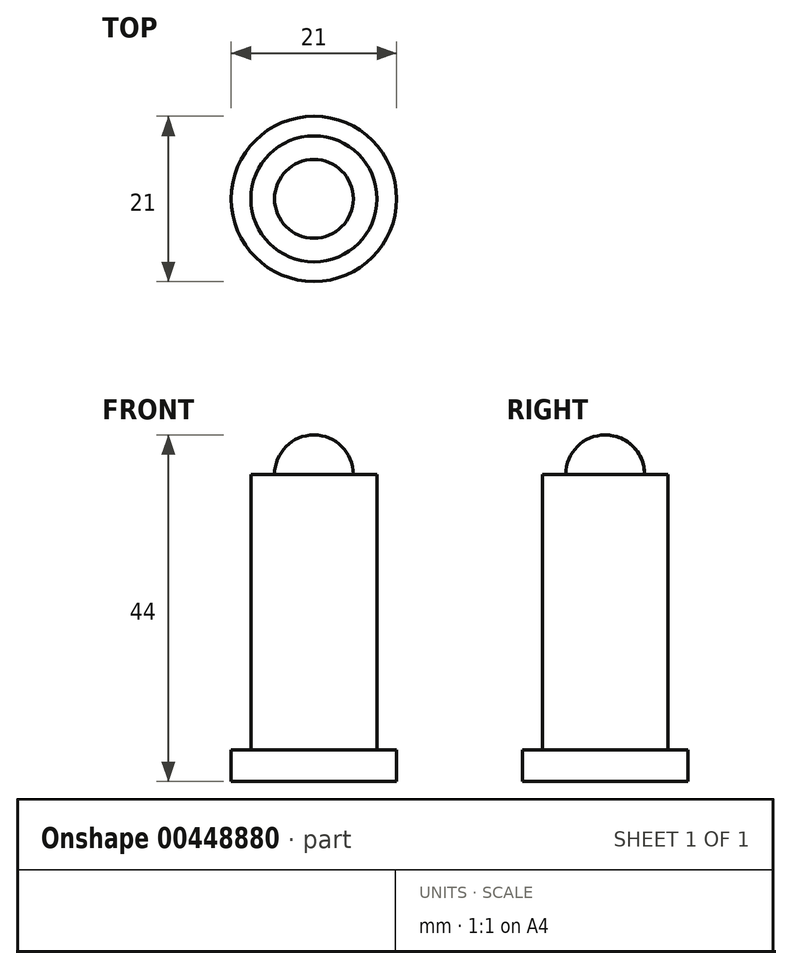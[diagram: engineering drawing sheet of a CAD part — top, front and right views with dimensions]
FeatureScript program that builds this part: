
annotation { "Feature Type Name" : "Feature", "Feature Type Description" : "" }
export const myFeature = defineFeature(function(context is Context, id is Id, definition is map)
    precondition{}
    {
        {
            var Q0;
            Q0=qCreatedBy(makeId("Top.planeOp"),FACE);
            var sketch = newSketch(context, id + "F0", { "sketchPlane" : qUnion([Q0])});
            skCircle(sketch, "E0", {"center": v(0, 0) * mm, "radius": 10.5 * mm});
            skSolve(sketch);
        }
        {
            var Q0;
            Q0=qSketchRegion(id+"F0",true);
            extrude(context, id + "F1", {"entities" : qUnion([Q0]), "depth" : 4 * mm});
        }
        {
            var Q0;
            Q0=qCreatedBy(makeId("Top.planeOp"),FACE);
            var sketch = newSketch(context, id + "F2", { "sketchPlane" : qUnion([Q0])});
            skCircle(sketch, "E1", {"center": v(0, 0) * mm, "radius": 8 * mm});
            skSolve(sketch);
        }
        {
            var Q0;
            Q0=qSketchRegion(id+"F2",true);
            extrude(context, id + "F3", {"entities" : qUnion([Q0]), "operationType" : NewBodyOperationType.ADD, "depth" : 39 * mm});
        }
        {
            var Q0;
            Q0=qCreatedBy(makeId("Right.planeOp"),FACE);
            var sketch = newSketch(context, id + "F4", { "sketchPlane" : qUnion([Q0])});
            skLineSegment(sketch, "E2", {"start": v(0, 44) * mm, "end": v(0, 39) * mm});
            skLineSegment(sketch, "E3", {"start": v(0, 39) * mm, "end": v(5, 39) * mm});
            skArc(sketch, "E4", {"start": v(5, 39) * mm, "mid": v(3.54, 42.54) * mm, "end": v(0, 44) * mm});
            skSolve(sketch);
        }
        {
            var Q0;
            Q0=makeQuery(id+"F4.imprint","IMPRINT",FACE,{"disambiguationData":[TD([[makeQuery(id+"F4.imprint","IMPRINT",EDGE,{"derivedFrom":sQuery(id+"F4.wireOp",EDGE,"E2")}),1.0]])]});
            var Q1;
            {var subQ4=sQuery(id+"F4.wireOp",EDGE,"bCaXd63Z-sSvQ-xuQP-ZVX1-OTuKCmXqE8nU");Q1=makeQuery(id+"F4.imprint","IMPRINT",FACE,{"disambiguationData":[TD([[makeQuery(id+"F4.imprint","IMPRINT",EDGE,{"derivedFrom":subQ4}),1.0]])]});}
            var Q2;
            {var subQ3=sQuery(id+"F4.wireOp",EDGE,"1d30ehnV-xLIY-fLZD-29Qb-ZKUb7VrrrgXH");Q2=makeQuery(id+"F4.imprint","IMPRINT",FACE,{"disambiguationData":[TD([[makeQuery(id+"F4.imprint","IMPRINT",EDGE,{"derivedFrom":subQ3}),1.0]])]});}
            var Q3;
            Q3=sQuery(id+"F4.wireOp",EDGE,"E2");
            revolve(context, id + "F5", {"operationType" : NewBodyOperationType.ADD, "entities" : qUnion([Q0, Q1, Q2]), "axis" : qUnion([Q3]), "revolveType" : RevolveType.FULL});
        }
    });
